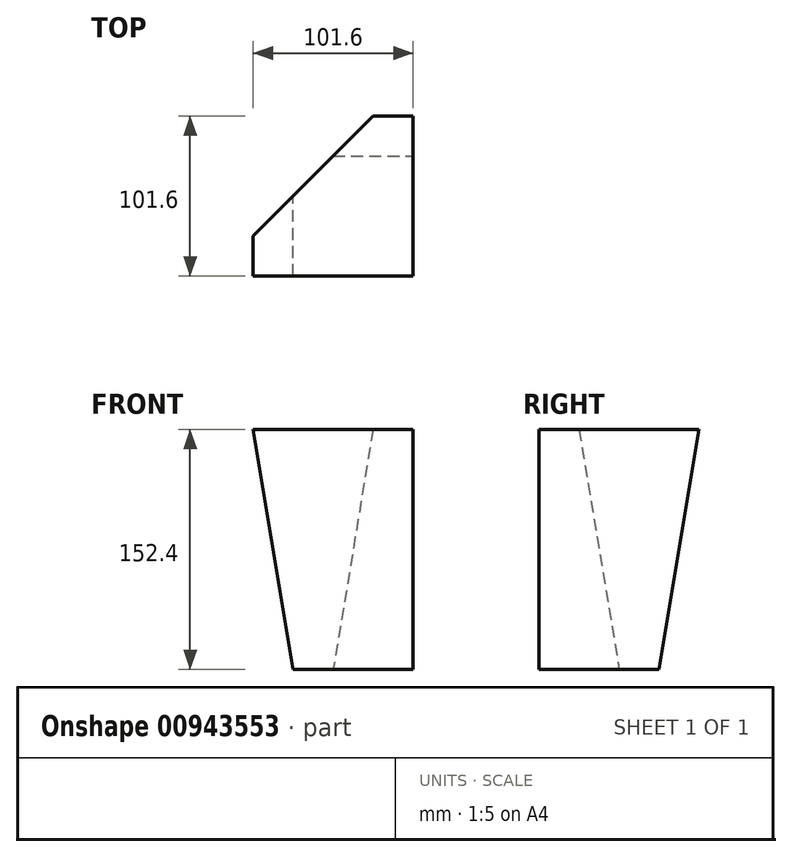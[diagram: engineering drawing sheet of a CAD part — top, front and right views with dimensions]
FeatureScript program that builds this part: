
annotation { "Feature Type Name" : "Feature", "Feature Type Description" : "" }
export const myFeature = defineFeature(function(context is Context, id is Id, definition is map)
    precondition{}
    {
        {
            var Q0;
            Q0=qCreatedBy(makeId("Top.planeOp"),FACE);
            var sketch = newSketch(context, id + "F0", { "sketchPlane" : qUnion([Q0])});
            skLineSegment(sketch, "E0.bottom", {"start": v(0, 0) * mm, "end": v(76.2, 0) * mm});
            skLineSegment(sketch, "E0.top", {"start": v(0, 76.2) * mm, "end": v(76.2, 76.2) * mm});
            skLineSegment(sketch, "E0.left", {"start": v(0, 0) * mm, "end": v(0, 76.2) * mm});
            skLineSegment(sketch, "E0.right", {"start": v(76.2, 0) * mm, "end": v(76.2, 76.2) * mm});
            skLineSegment(sketch, "E1", {"start": v(25.4, 76.2) * mm, "end": v(0, 50.8) * mm});
            skSolve(sketch);
        }
        {
            var Q0;
            Q0=qCreatedBy(makeId("Top.planeOp"),FACE);
            cPlane(context, id + "F1", {"entities" : qUnion([Q0]), "cplaneType" : CPlaneType.OFFSET, "offset" : 152.4 * mm, "width" : 152.4 * mm, "height" : 152.4 * mm});
        }
        {
            var Q0;
            Q0=qCreatedBy(id+"F1.planeOp",FACE);
            var sketch = newSketch(context, id + "F2", { "sketchPlane" : qUnion([Q0])});
            skLineSegment(sketch, "E2.bottom", {"start": v(76.2, 0) * mm, "end": v(-25.4, 0) * mm});
            skLineSegment(sketch, "E2.top", {"start": v(76.2, 101.6) * mm, "end": v(-25.4, 101.6) * mm});
            skLineSegment(sketch, "E2.left", {"start": v(76.2, 0) * mm, "end": v(76.2, 101.6) * mm});
            skLineSegment(sketch, "E2.right", {"start": v(-25.4, 0) * mm, "end": v(-25.4, 101.6) * mm});
            skLineSegment(sketch, "E3", {"start": v(50.8, 101.6) * mm, "end": v(-25.4, 25.4) * mm});
            skSolve(sketch);
        }
        {
            var Q0;
            {var subQ1=sQuery(id+"F2.wireOp",EDGE,"E2.bottom");Q0=makeQuery(id+"F2.imprint","IMPRINT",FACE,{"disambiguationData":[TD([[makeQuery(id+"F2.imprint","IMPRINT",EDGE,{"derivedFrom":subQ1}),-1.0]])]});}
            var Q1;
            {var subQ1=sQuery(id+"F0.wireOp",EDGE,"E0.bottom");Q1=makeQuery(id+"F0.imprint","IMPRINT",FACE,{"disambiguationData":[TD([[makeQuery(id+"F0.imprint","IMPRINT",EDGE,{"derivedFrom":subQ1}),1.0]])]});}
            loft(context, id + "F3", {"sheetProfilesArray" : [{ "sheetProfileEntities" : qUnion([Q0]) }, { "sheetProfileEntities" : qUnion([Q1]) }]});
        }
    });
